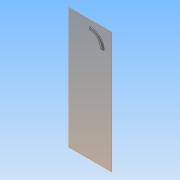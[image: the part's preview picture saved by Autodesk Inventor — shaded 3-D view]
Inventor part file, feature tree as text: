
AUTODESK INVENTOR PART (.ipt)
format: ipt  version: 2013 (Build 170138000, 138)  size: 118,784 bytes
history: native  units: in
note: dims shown in document units (in); Inventor stores cm internally (conversion verified against a paired STEP export)
features: reference x4, extrude x2, sketch x2, plane x1
ambient origin geometry x8: Origin, YZ Plane, XZ Plane, XY Plane, X Axis, Y Axis, Z Axis, Center Point
bodies: Solid1 (feature_tree)
feature tree (9):
  plane  "Work Plane1"
  extrude  "Extrusion1"  Depth=0.71in TaperAngle=0.0deg
  extrude  "Extrusion2"  Depth=0.5in TaperAngle=0.0deg
  sketch  "Sketch1"  dims[d0=12.0in d1=0.71in d2=0.0in]
  reference  "Reference1"
  reference  "Reference2"
  reference  "Reference3"
  sketch  "Sketch2"  dims[d3=0.5in d5=0.5in d6=0.0in]
  reference  "Reference4"
